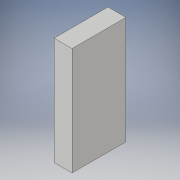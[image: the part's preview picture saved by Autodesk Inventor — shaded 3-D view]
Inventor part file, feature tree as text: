
AUTODESK INVENTOR PART (.ipt)
format: ipt  version: 2017 (Build 210142000, 142)  size: 87,552 bytes
history: native  units: in
note: dims shown in document units (in); Inventor stores cm internally (conversion verified against a paired STEP export)
features: extrude x1, sketch x1
ambient origin geometry x8: Origin, YZ Plane, XZ Plane, XY Plane, X Axis, Y Axis, Z Axis, Center Point
bodies: Solid1 (feature_tree)
feature tree (2):
  extrude  "Extrusion1"  Depth=3.0in
  sketch  "Sketch1"  dims[d0=6.0in d1=3.0in d2=1.0in d3=0.0in]
